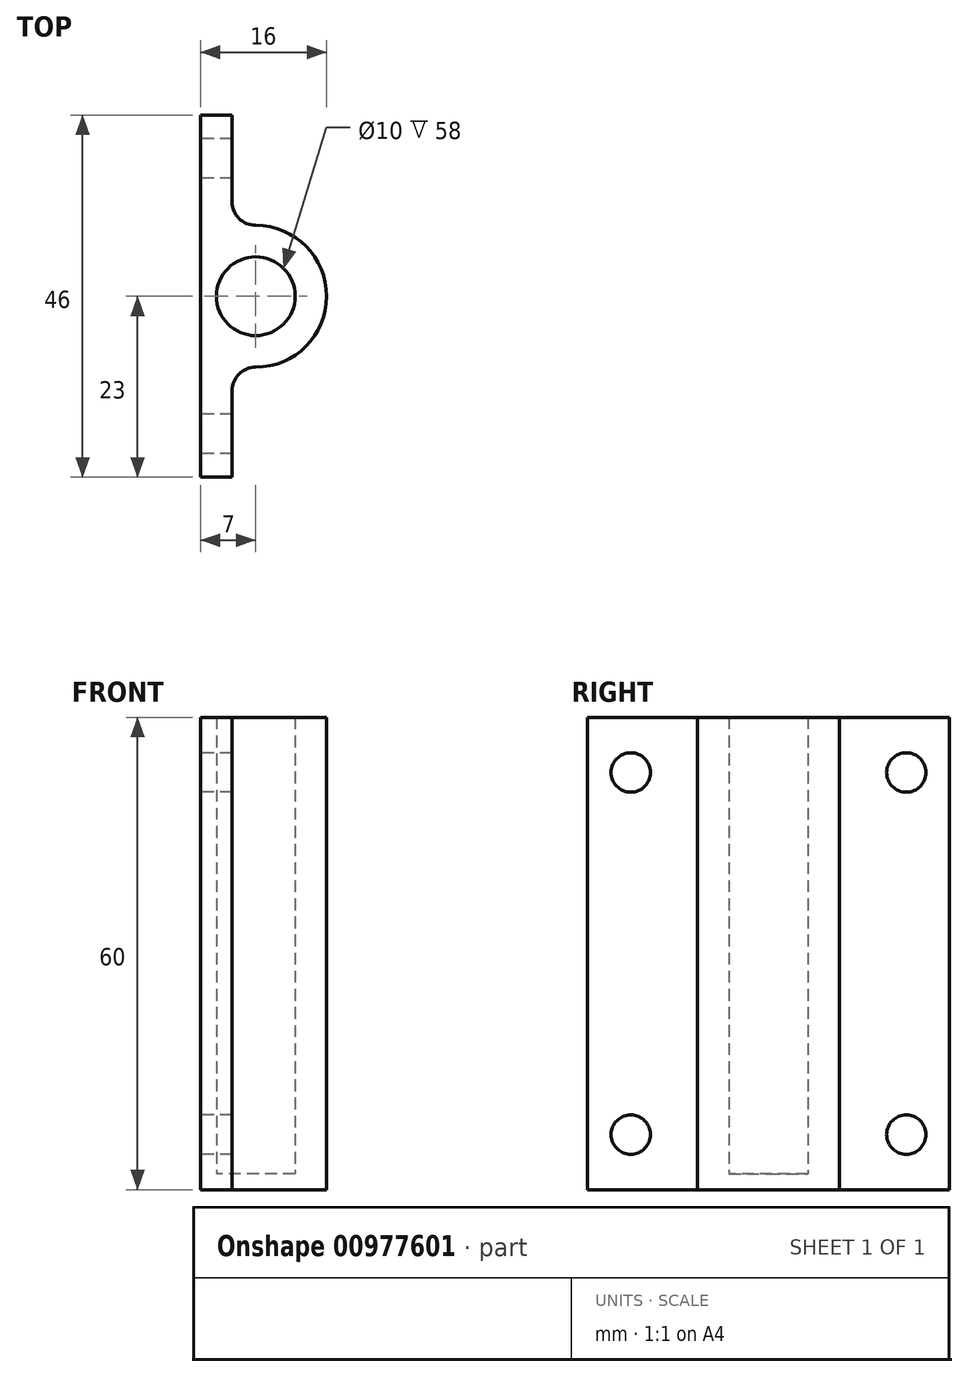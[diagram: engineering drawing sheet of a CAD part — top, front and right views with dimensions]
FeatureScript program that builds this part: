
annotation { "Feature Type Name" : "Feature", "Feature Type Description" : "" }
export const myFeature = defineFeature(function(context is Context, id is Id, definition is map)
    precondition{}
    {
        {
            var Q0;
            Q0=qCreatedBy(makeId("Top.planeOp"),FACE);
            var sketch = newSketch(context, id + "F0", { "sketchPlane" : qUnion([Q0])});
            skCircle(sketch, "E0", {"center": v(0, 0) * mm, "radius": 5 * mm});
            skArc(sketch, "E1", {"start": v(0, -9) * mm, "mid": v(9, 0) * mm, "end": v(0, 9) * mm});
            skLineSegment(sketch, "E2.bottom", {"start": v(-7, 23) * mm, "end": v(-3, 23) * mm});
            skLineSegment(sketch, "E2.top", {"start": v(-7, -23) * mm, "end": v(-3, -23) * mm});
            skLineSegment(sketch, "E2.left", {"start": v(-7, 23) * mm, "end": v(-7, -23) * mm});
            skLineSegment(sketch, "E2.right", {"start": v(-3, 23) * mm, "end": v(-3, 12) * mm});
            skPoint(sketch, "E2.middle", {"position": v(-5, 0) * mm});
            skPoint(sketch, "E3.newPointB", {"position": v(0, 9) * mm});
            skArc(sketch, "E3.filletArc", {"start": v(-3, 12) * mm, "mid": v(-2.12, 9.88) * mm, "end": v(0, 9) * mm});
            skLineSegment(sketch, "E4", {"start": v(-3, -23) * mm, "end": v(-3, -12) * mm});
            skPoint(sketch, "E5.newPointB", {"position": v(0, -9) * mm});
            skArc(sketch, "E5.filletArc", {"start": v(0, -9) * mm, "mid": v(-2.12, -9.88) * mm, "end": v(-3, -12) * mm});
            skSolve(sketch);
        }
        {
            var Q0;
            Q0=makeQuery(id+"F0.imprint","IMPRINT",FACE,{"disambiguationData":[TD([[makeQuery(id+"F0.imprint","IMPRINT",EDGE,{"derivedFrom":sQuery(id+"F0.wireOp",EDGE,"E0")}),-1.0]])]});
            var Q1;
            Q1=makeQuery(id+"F0.imprint","IMPRINT",FACE,{"disambiguationData":[TD([[makeQuery(id+"F0.imprint","IMPRINT",EDGE,{"derivedFrom":sQuery(id+"F0.wireOp",EDGE,"E0")}),1.0]])]});
            extrude(context, id + "F1", {"entities" : qUnion([Q0, Q1]), "depth" : 2 * mm, "offsetDistance" : 25 * mm});
        }
        {
            var Q0;
            Q0=makeQuery(id+"F1.opExtrude","CAP_FACE",FACE,{"disambiguationData":[OSD([sQuery(id+"F0.wireOp",EDGE,"E1"),sQuery(id+"F0.wireOp",EDGE,"E2.bottom"),sQuery(id+"F0.wireOp",EDGE,"E2.top"),sQuery(id+"F0.wireOp",EDGE,"E2.left"),sQuery(id+"F0.wireOp",EDGE,"E2.right"),sQuery(id+"F0.wireOp",EDGE,"E3.filletArc"),sQuery(id+"F0.wireOp",EDGE,"E4"),sQuery(id+"F0.wireOp",EDGE,"E5.filletArc")])],"isStart":false});
            var sketch = newSketch(context, id + "F2", { "sketchPlane" : qUnion([Q0])});
            skCircle(sketch, "E6", {"center": v(0, 0) * mm, "radius": 5 * mm});
            skArc(sketch, "E7", {"start": v(0, -9) * mm, "mid": v(9, 0) * mm, "end": v(0, 9) * mm});
            skLineSegment(sketch, "E8.bottom", {"start": v(-7, 23) * mm, "end": v(-3, 23) * mm});
            skLineSegment(sketch, "E8.top", {"start": v(-7, -23) * mm, "end": v(-3, -23) * mm});
            skLineSegment(sketch, "E8.left", {"start": v(-7, 23) * mm, "end": v(-7, -23) * mm});
            skLineSegment(sketch, "E8.right", {"start": v(-3, 23) * mm, "end": v(-3, 12) * mm});
            skPoint(sketch, "E8.middle", {"position": v(-5, 0) * mm});
            skPoint(sketch, "E9.newPointB", {"position": v(0, 9) * mm});
            skArc(sketch, "E9.filletArc", {"start": v(-3, 12) * mm, "mid": v(-2.12, 9.88) * mm, "end": v(0, 9) * mm});
            skLineSegment(sketch, "E10", {"start": v(-3, -23) * mm, "end": v(-3, -12) * mm});
            skPoint(sketch, "E11.newPointB", {"position": v(0, -9) * mm});
            skArc(sketch, "E11.filletArc", {"start": v(0, -9) * mm, "mid": v(-2.12, -9.88) * mm, "end": v(-3, -12) * mm});
            skSolve(sketch);
        }
        {
            var Q0;
            Q0=makeQuery(id+"F2.imprint","IMPRINT",FACE,{"disambiguationData":[TD([[makeQuery(id+"F2.imprint","IMPRINT",EDGE,{"derivedFrom":sQuery(id+"F2.wireOp",EDGE,"E6")}),-1.0]])]});
            extrude(context, id + "F3", {"entities" : qUnion([Q0]), "operationType" : NewBodyOperationType.ADD, "depth" : 58 * mm, "offsetDistance" : 25 * mm});
        }
        {
            var Q0;
            Q0=makeQuery(id+"F3.boolean.opBoolean","MERGE",FACE,{"derivedFrom":[makeQuery(id+"F1.opExtrude","SWEPT_FACE",FACE,{"disambiguationData":[OSD([sQuery(id+"F0.wireOp",EDGE,"E2.left")])]}),makeQuery(id+"F3.opExtrude","SWEPT_FACE",FACE,{"disambiguationData":[OSD([sQuery(id+"F2.wireOp",EDGE,"96dadd9d-1d75-4087-997d-d517ea428045.left")])]})]});
            var sketch = newSketch(context, id + "F4", { "sketchPlane" : qUnion([Q0])});
            skLineSegment(sketch, "E12.bottom", {"start": v(-23, 60) * mm, "end": v(-17.5, 60) * mm, "construction": true});
            skLineSegment(sketch, "E12.top", {"start": v(-23, 53) * mm, "end": v(-17.5, 53) * mm, "construction": true});
            skLineSegment(sketch, "E12.left", {"start": v(-23, 60) * mm, "end": v(-23, 53) * mm, "construction": true});
            skLineSegment(sketch, "E12.right", {"start": v(-17.5, 60) * mm, "end": v(-17.5, 53) * mm, "construction": true});
            skLineSegment(sketch, "E13.bottom", {"start": v(23, 60) * mm, "end": v(17.5, 60) * mm, "construction": true});
            skLineSegment(sketch, "E13.top", {"start": v(23, 53) * mm, "end": v(17.5, 53) * mm, "construction": true});
            skLineSegment(sketch, "E13.left", {"start": v(23, 60) * mm, "end": v(23, 53) * mm, "construction": true});
            skLineSegment(sketch, "E13.right", {"start": v(17.5, 60) * mm, "end": v(17.5, 53) * mm, "construction": true});
            skLineSegment(sketch, "E14.bottom", {"start": v(-23, 0) * mm, "end": v(-17.5, 0) * mm, "construction": true});
            skLineSegment(sketch, "E14.top", {"start": v(-23, 7) * mm, "end": v(-17.5, 7) * mm, "construction": true});
            skLineSegment(sketch, "E14.left", {"start": v(-23, 0) * mm, "end": v(-23, 7) * mm, "construction": true});
            skLineSegment(sketch, "E14.right", {"start": v(-17.5, 0) * mm, "end": v(-17.5, 7) * mm, "construction": true});
            skLineSegment(sketch, "E15.bottom", {"start": v(23, 0) * mm, "end": v(17.5, 0) * mm, "construction": true});
            skLineSegment(sketch, "E15.top", {"start": v(23, 7) * mm, "end": v(17.5, 7) * mm, "construction": true});
            skLineSegment(sketch, "E15.left", {"start": v(23, 0) * mm, "end": v(23, 7) * mm, "construction": true});
            skLineSegment(sketch, "E15.right", {"start": v(17.5, 0) * mm, "end": v(17.5, 7) * mm, "construction": true});
            skCircle(sketch, "E16", {"center": v(-17.5, 53) * mm, "radius": 2.5 * mm});
            skCircle(sketch, "E17", {"center": v(17.5, 53) * mm, "radius": 2.5 * mm});
            skCircle(sketch, "E18", {"center": v(-17.5, 7) * mm, "radius": 2.5 * mm});
            skCircle(sketch, "E19", {"center": v(17.5, 7) * mm, "radius": 2.5 * mm});
            skSolve(sketch);
        }
        {
            var Q0;
            Q0=makeQuery(id+"F4.imprint","IMPRINT",FACE,{"disambiguationData":[TD([[makeQuery(id+"F4.imprint","IMPRINT",EDGE,{"derivedFrom":sQuery(id+"F4.wireOp",EDGE,"E16")}),1.0]])]});
            var Q1;
            Q1=makeQuery(id+"F4.imprint","IMPRINT",FACE,{"disambiguationData":[TD([[makeQuery(id+"F4.imprint","IMPRINT",EDGE,{"derivedFrom":sQuery(id+"F4.wireOp",EDGE,"E19")}),1.0]])]});
            var Q2;
            Q2=makeQuery(id+"F4.imprint","IMPRINT",FACE,{"disambiguationData":[TD([[makeQuery(id+"F4.imprint","IMPRINT",EDGE,{"derivedFrom":sQuery(id+"F4.wireOp",EDGE,"E18")}),1.0]])]});
            var Q3;
            Q3=makeQuery(id+"F4.imprint","IMPRINT",FACE,{"disambiguationData":[TD([[makeQuery(id+"F4.imprint","IMPRINT",EDGE,{"derivedFrom":sQuery(id+"F4.wireOp",EDGE,"E17")}),1.0]])]});
            extrude(context, id + "F5", {"entities" : qUnion([Q0, Q1, Q2, Q3]), "operationType" : NewBodyOperationType.REMOVE, "oppositeDirection" : true, "depth" : 10 * mm, "offsetDistance" : 25 * mm});
        }
    });
